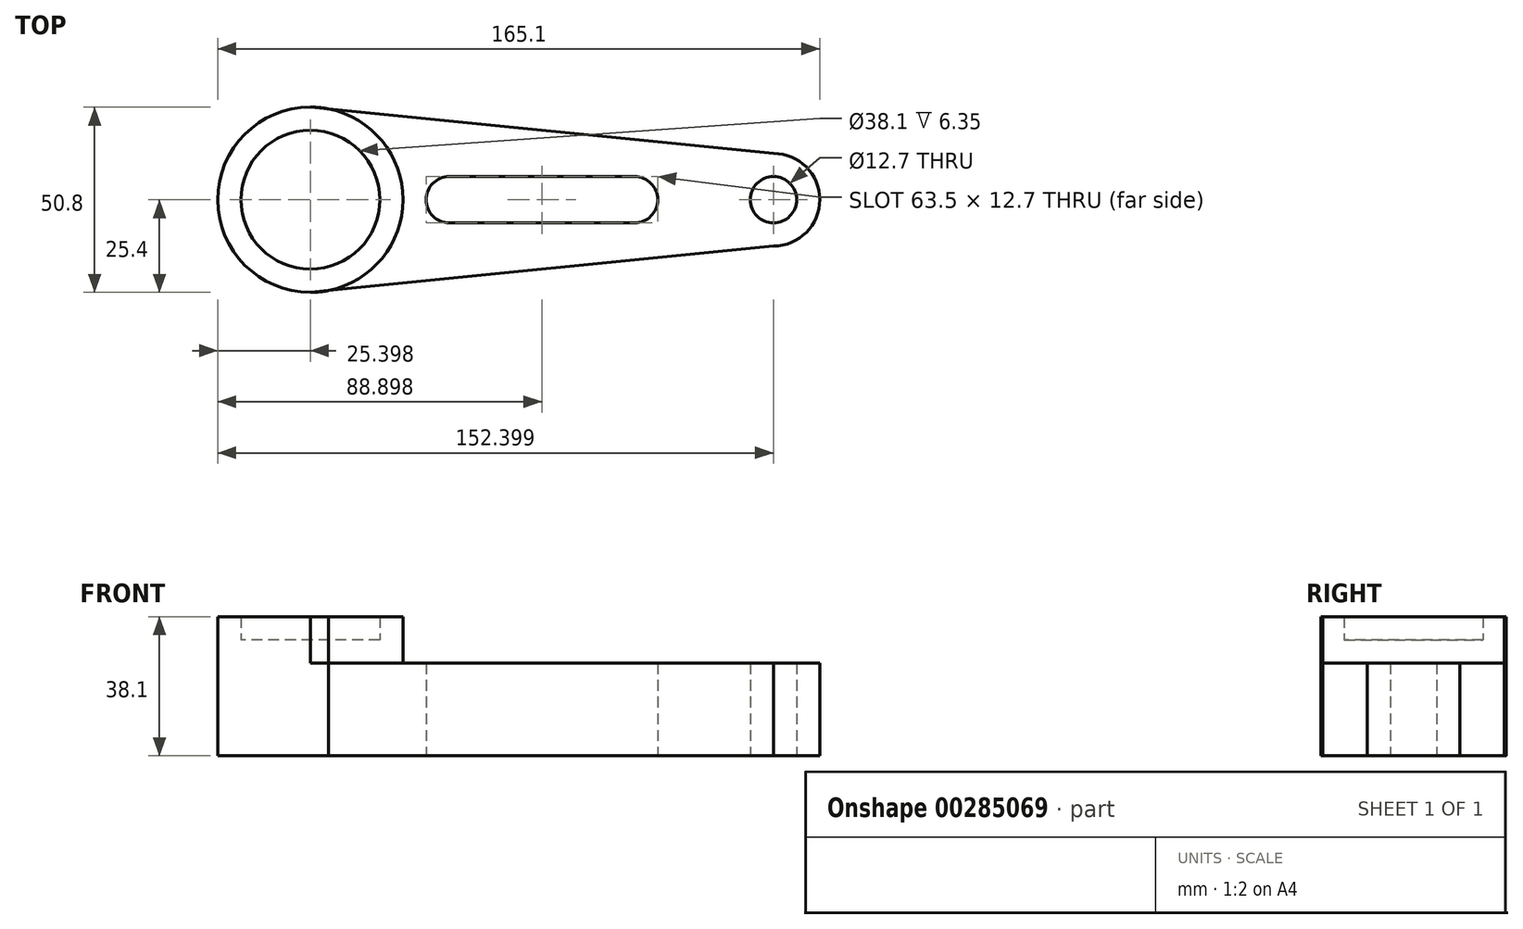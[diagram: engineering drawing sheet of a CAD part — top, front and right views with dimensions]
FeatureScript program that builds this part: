
annotation { "Feature Type Name" : "Feature", "Feature Type Description" : "" }
export const myFeature = defineFeature(function(context is Context, id is Id, definition is map)
    precondition{}
    {
        {
            var Q0;
            Q0=qCreatedBy(makeId("Top.planeOp"),FACE);
            var sketch = newSketch(context, id + "F0", { "sketchPlane" : qUnion([Q0])});
            skCircle(sketch, "E0", {"center": v(-89.93, 0) * mm, "radius": 25.4 * mm});
            skCircle(sketch, "E1", {"center": v(-89.93, 0) * mm, "radius": 19.05 * mm});
            skCircle(sketch, "E2", {"center": v(37.07, 0) * mm, "radius": 6.35 * mm});
            skCircle(sketch, "E3", {"center": v(37.07, 0) * mm, "radius": 12.7 * mm});
            skLineSegment(sketch, "E4", {"start": v(-51.83, 6.35) * mm, "end": v(-1.03, 6.35) * mm});
            skLineSegment(sketch, "E5", {"start": v(-89.93, -25.4) * mm, "end": v(37.07, -12.7) * mm});
            skLineSegment(sketch, "E6", {"start": v(-89.93, 25.4) * mm, "end": v(37.07, 12.7) * mm});
            skLineSegment(sketch, "E7", {"start": v(-51.83, -6.35) * mm, "end": v(-1.03, -6.35) * mm});
            skArc(sketch, "E8", {"start": v(-1.03, -6.35) * mm, "mid": v(5.32, 0) * mm, "end": v(-1.03, 6.35) * mm});
            skArc(sketch, "E9", {"start": v(-51.83, 6.35) * mm, "mid": v(-58.18, 0) * mm, "end": v(-51.83, -6.35) * mm});
            skSolve(sketch);
        }
        {
            var Q0;
            Q0=makeQuery(id+"F0.imprint","IMPRINT",FACE,{"disambiguationData":[TD([[makeQuery(id+"F0.imprint","IMPRINT",EDGE,{"derivedFrom":sQuery(id+"F0.wireOp",EDGE,"E1")}),-1.0]])]});
            extrude(context, id + "F1", {"entities" : qUnion([Q0]), "depth" : 38.1 * mm});
        }
        {
            var Q0;
            Q0=makeQuery(id+"F0.imprint","IMPRINT",FACE,{"disambiguationData":[TD([[makeQuery(id+"F0.imprint","IMPRINT",EDGE,{"derivedFrom":sQuery(id+"F0.wireOp",EDGE,"E1")}),1.0]])]});
            extrude(context, id + "F2", {"entities" : qUnion([Q0]), "operationType" : NewBodyOperationType.ADD, "depth" : 31.75 * mm});
        }
        {
            var Q0;
            Q0 = qSketchRegion(id + "F0", true);
            extrude(context, id + "F3", {"entities" : qUnion([Q0]), "operationType" : NewBodyOperationType.ADD, "depth" : 25.4 * mm});
        }
    });
